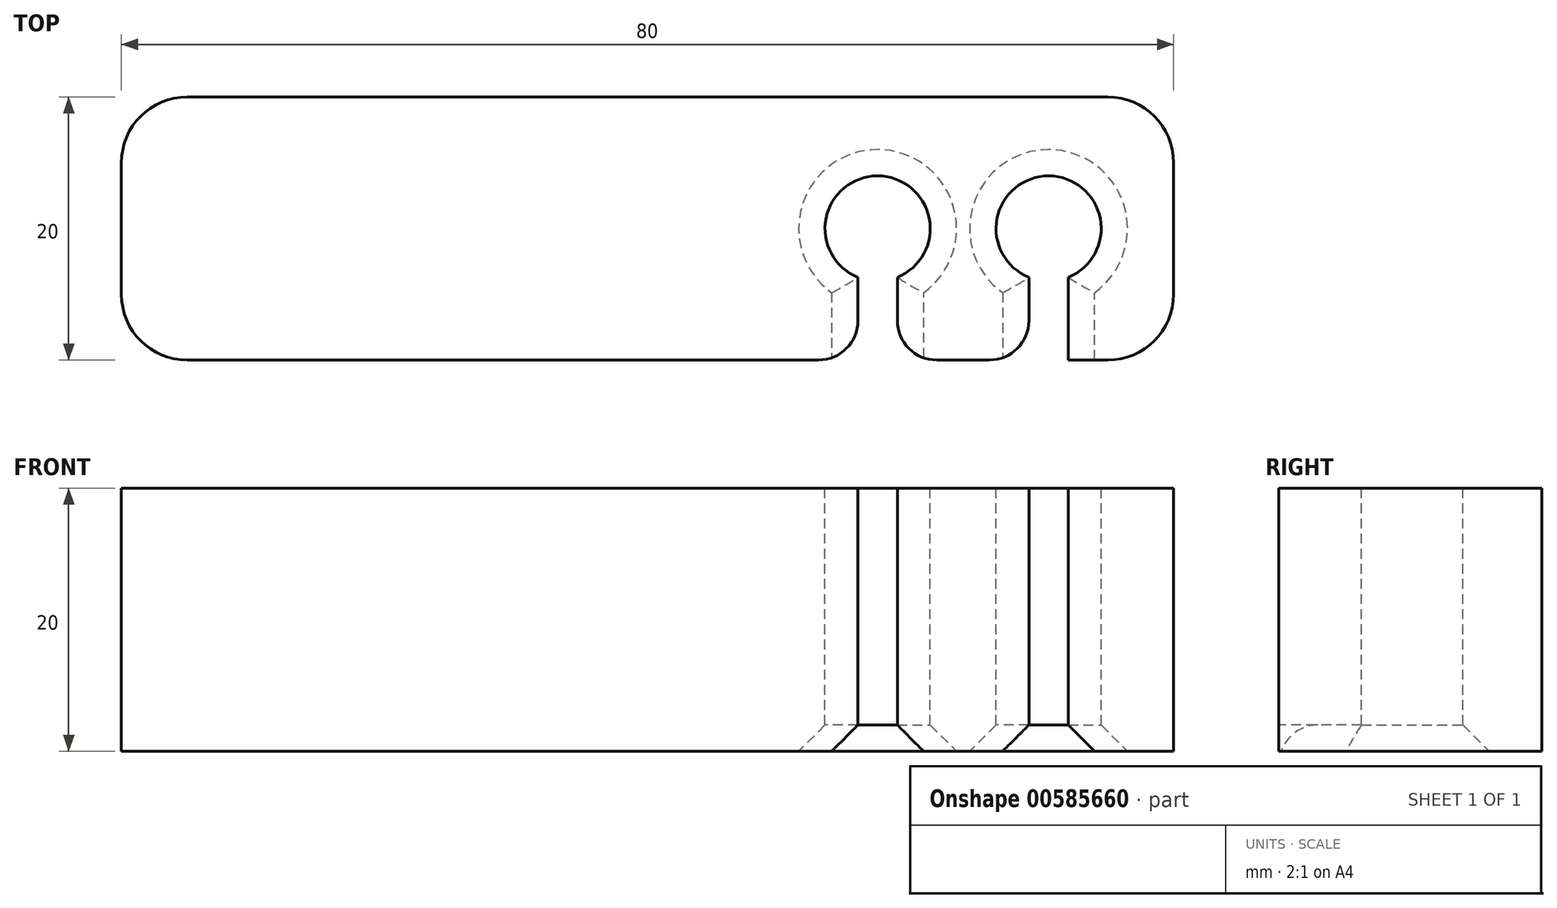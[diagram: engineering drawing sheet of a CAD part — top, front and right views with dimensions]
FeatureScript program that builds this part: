
annotation { "Feature Type Name" : "Feature", "Feature Type Description" : "" }
export const myFeature = defineFeature(function(context is Context, id is Id, definition is map)
    precondition{}
    {
        {
            var Q0;
            Q0=qCreatedBy(makeId("Top.planeOp"),FACE);
            var sketch = newSketch(context, id + "F0", { "sketchPlane" : qUnion([Q0])});
            skLineSegment(sketch, "E0.bottom", {"start": v(40, -10) * mm, "end": v(-40, -10) * mm});
            skLineSegment(sketch, "E0.top", {"start": v(40, 10) * mm, "end": v(-40, 10) * mm});
            skLineSegment(sketch, "E0.left", {"start": v(40, -10) * mm, "end": v(40, 10) * mm});
            skLineSegment(sketch, "E0.right", {"start": v(-40, -10) * mm, "end": v(-40, 10) * mm});
            skPoint(sketch, "E0.middle", {"position": v(0, 0) * mm});
            skSolve(sketch);
        }
        {
            var Q0;
            Q0 = qSketchRegion(id + "F0", true);
            extrude(context, id + "F1", {"entities" : qUnion([Q0]), "depth" : 20 * mm, "offsetDistance" : 25 * mm});
        }
        {
            var Q0;
            Q0=makeQuery(id+"F1.opExtrude","CAP_FACE",FACE,{"disambiguationData":[OSD([sQuery(id+"F0.wireOp",EDGE,"E0.bottom"),sQuery(id+"F0.wireOp",EDGE,"E0.top"),sQuery(id+"F0.wireOp",EDGE,"E0.left"),sQuery(id+"F0.wireOp",EDGE,"E0.right")])],"isStart":false});
            var sketch = newSketch(context, id + "F2", { "sketchPlane" : qUnion([Q0])});
            skLineSegment(sketch, "E1.bottom", {"start": v(32, -10) * mm, "end": v(29, -10) * mm});
            skLineSegment(sketch, "E1.top", {"start": v(32, 0) * mm, "end": v(29, 0) * mm, "construction": true});
            skLineSegment(sketch, "E1.left", {"start": v(32, -10) * mm, "end": v(32, 0) * mm});
            skLineSegment(sketch, "E1.right", {"start": v(29, -10) * mm, "end": v(29, 0) * mm});
            skLineSegment(sketch, "E2.bottom", {"start": v(19, -10) * mm, "end": v(16, -10) * mm});
            skLineSegment(sketch, "E2.top", {"start": v(19, 0) * mm, "end": v(16, 0) * mm, "construction": true});
            skLineSegment(sketch, "E2.left", {"start": v(19, -10) * mm, "end": v(19, 0) * mm});
            skLineSegment(sketch, "E2.right", {"start": v(16, -10) * mm, "end": v(16, 0) * mm});
            skLineSegment(sketch, "E3", {"start": v(19, 0) * mm, "end": v(29, 0) * mm, "construction": true});
            skArc(sketch, "E4", {"start": v(19, 0) * mm, "mid": v(17.5, 1.5) * mm, "end": v(16, 0) * mm});
            skArc(sketch, "E5", {"start": v(32, 0) * mm, "mid": v(30.5, 1.5) * mm, "end": v(29, 0) * mm});
            skSolve(sketch);
        }
        {
            var Q0;
            Q0 = qSketchRegion(id + "F2", true);
            extrude(context, id + "F3", {"entities" : qUnion([Q0]), "operationType" : NewBodyOperationType.REMOVE, "endBound" : BoundingType.THROUGH_ALL, "oppositeDirection" : true, "depth" : 25 * mm, "offsetDistance" : 25 * mm});
        }
        {
            var Q0;
            Q0=makeQuery(id+"F1.opExtrude","CAP_FACE",FACE,{"disambiguationData":[OSD([sQuery(id+"F0.wireOp",EDGE,"E0.bottom"),sQuery(id+"F0.wireOp",EDGE,"E0.top"),sQuery(id+"F0.wireOp",EDGE,"E0.left"),sQuery(id+"F0.wireOp",EDGE,"E0.right")])],"isStart":false});
            var sketch = newSketch(context, id + "F4", { "sketchPlane" : qUnion([Q0])});
            skCircle(sketch, "E6", {"center": v(17.5, 0) * mm, "radius": 4 * mm});
            skCircle(sketch, "E7", {"center": v(30.5, 0) * mm, "radius": 4 * mm});
            skSolve(sketch);
        }
        {
            var Q0;
            Q0 = qSketchRegion(id + "F4", true);
            extrude(context, id + "F5", {"entities" : qUnion([Q0]), "operationType" : NewBodyOperationType.REMOVE, "endBound" : BoundingType.THROUGH_ALL, "oppositeDirection" : true, "depth" : 25 * mm, "offsetDistance" : 25 * mm});
        }
        {
            var Q0;
            Q0=makeQuery(id+"F5.boolean.opBoolean","COPY",EDGE,{"derivedFrom":makeQuery(id+"F5.opExtrude","CAP_EDGE",EDGE,{"disambiguationData":[OSD([sQuery(id+"F4.wireOp",EDGE,"E6")])],"isStart":true})});
            var Q1;
            Q1=makeQuery(id+"F5.boolean.opBoolean","COPY",EDGE,{"derivedFrom":makeQuery(id+"F5.opExtrude","CAP_EDGE",EDGE,{"disambiguationData":[OSD([sQuery(id+"F4.wireOp",EDGE,"E7")])],"isStart":true})});
            var Q2;
            Q2=makeQuery(id+"F5.boolean.opBoolean","INTERSECT",EDGE,{"derivedFrom":[makeQuery(id+"F1.opExtrude","CAP_FACE",FACE,{"disambiguationData":[OSD([sQuery(id+"F0.wireOp",EDGE,"E0.bottom"),sQuery(id+"F0.wireOp",EDGE,"E0.top"),sQuery(id+"F0.wireOp",EDGE,"E0.left"),sQuery(id+"F0.wireOp",EDGE,"E0.right")])],"isStart":true}),makeQuery(id+"F5.opExtrude","SWEPT_FACE",FACE,{"disambiguationData":[OSD([sQuery(id+"F4.wireOp",EDGE,"E6")])]})]});
            var Q3;
            Q3=makeQuery(id+"F5.boolean.opBoolean","INTERSECT",EDGE,{"derivedFrom":[makeQuery(id+"F1.opExtrude","CAP_FACE",FACE,{"disambiguationData":[OSD([sQuery(id+"F0.wireOp",EDGE,"E0.bottom"),sQuery(id+"F0.wireOp",EDGE,"E0.top"),sQuery(id+"F0.wireOp",EDGE,"E0.left"),sQuery(id+"F0.wireOp",EDGE,"E0.right")])],"isStart":true}),makeQuery(id+"F5.opExtrude","SWEPT_FACE",FACE,{"disambiguationData":[OSD([sQuery(id+"F4.wireOp",EDGE,"E7")])]})]});
            var Q4;
            Q4=makeQuery(id+"F3.boolean.opBoolean","COPY",EDGE,{"derivedFrom":makeQuery(id+"F3.opExtrude","CAP_EDGE",EDGE,{"disambiguationData":[OSD([sQuery(id+"F2.wireOp",EDGE,"E2.right")])],"isStart":true})});
            var Q5;
            Q5=makeQuery(id+"F3.boolean.opBoolean","COPY",EDGE,{"derivedFrom":makeQuery(id+"F3.opExtrude","CAP_EDGE",EDGE,{"disambiguationData":[OSD([sQuery(id+"F2.wireOp",EDGE,"E2.left")])],"isStart":true})});
            var Q6;
            Q6=makeQuery(id+"F3.boolean.opBoolean","COPY",EDGE,{"derivedFrom":makeQuery(id+"F3.opExtrude","CAP_EDGE",EDGE,{"disambiguationData":[OSD([sQuery(id+"F2.wireOp",EDGE,"E1.right")])],"isStart":true})});
            var Q7;
            Q7=makeQuery(id+"F3.boolean.opBoolean","COPY",EDGE,{"derivedFrom":makeQuery(id+"F3.opExtrude","CAP_EDGE",EDGE,{"disambiguationData":[OSD([sQuery(id+"F2.wireOp",EDGE,"E1.left")])],"isStart":true})});
            var Q8;
            Q8=makeQuery(id+"F3.boolean.opBoolean","INTERSECT",EDGE,{"derivedFrom":[makeQuery(id+"F1.opExtrude","CAP_FACE",FACE,{"disambiguationData":[OSD([sQuery(id+"F0.wireOp",EDGE,"E0.bottom"),sQuery(id+"F0.wireOp",EDGE,"E0.top"),sQuery(id+"F0.wireOp",EDGE,"E0.left"),sQuery(id+"F0.wireOp",EDGE,"E0.right")])],"isStart":true}),makeQuery(id+"F3.opExtrude","SWEPT_FACE",FACE,{"disambiguationData":[OSD([sQuery(id+"F2.wireOp",EDGE,"E2.right")])]})]});
            var Q9;
            Q9=makeQuery(id+"F3.boolean.opBoolean","INTERSECT",EDGE,{"derivedFrom":[makeQuery(id+"F1.opExtrude","CAP_FACE",FACE,{"disambiguationData":[OSD([sQuery(id+"F0.wireOp",EDGE,"E0.bottom"),sQuery(id+"F0.wireOp",EDGE,"E0.top"),sQuery(id+"F0.wireOp",EDGE,"E0.left"),sQuery(id+"F0.wireOp",EDGE,"E0.right")])],"isStart":true}),makeQuery(id+"F3.opExtrude","SWEPT_FACE",FACE,{"disambiguationData":[OSD([sQuery(id+"F2.wireOp",EDGE,"E2.left")])]})]});
            var Q10;
            Q10=makeQuery(id+"F3.boolean.opBoolean","INTERSECT",EDGE,{"derivedFrom":[makeQuery(id+"F1.opExtrude","CAP_FACE",FACE,{"disambiguationData":[OSD([sQuery(id+"F0.wireOp",EDGE,"E0.bottom"),sQuery(id+"F0.wireOp",EDGE,"E0.top"),sQuery(id+"F0.wireOp",EDGE,"E0.left"),sQuery(id+"F0.wireOp",EDGE,"E0.right")])],"isStart":true}),makeQuery(id+"F3.opExtrude","SWEPT_FACE",FACE,{"disambiguationData":[OSD([sQuery(id+"F2.wireOp",EDGE,"E1.right")])]})]});
            var Q11;
            Q11=makeQuery(id+"F3.boolean.opBoolean","INTERSECT",EDGE,{"derivedFrom":[makeQuery(id+"F1.opExtrude","CAP_FACE",FACE,{"disambiguationData":[OSD([sQuery(id+"F0.wireOp",EDGE,"E0.bottom"),sQuery(id+"F0.wireOp",EDGE,"E0.top"),sQuery(id+"F0.wireOp",EDGE,"E0.left"),sQuery(id+"F0.wireOp",EDGE,"E0.right")])],"isStart":true}),makeQuery(id+"F3.opExtrude","SWEPT_FACE",FACE,{"disambiguationData":[OSD([sQuery(id+"F2.wireOp",EDGE,"E1.left")])]})]});
            chamfer(context, id + "F6", {"entities" : qUnion([Q0, Q1, Q2, Q3, Q4, Q5, Q6, Q7, Q8, Q9, Q10, Q11]), "width" : 2 * mm, "tangentPropagation" : true});
        }
        {
            var Q0;
            Q0=makeQuery(id+"F3.boolean.opBoolean","COPY",EDGE,{"derivedFrom":makeQuery(id+"F3.opExtrude","SWEPT_EDGE",EDGE,{"disambiguationData":[OSD([sQuery(id+"F0.wireOp",EDGE,"E0.bottom"),sQuery(id+"F2.wireOp",EDGE,"E2.bottom"),sQuery(id+"F2.wireOp",EDGE,"E2.left")])]})});
            var Q1;
            Q1=makeQuery(id+"F3.boolean.opBoolean","COPY",EDGE,{"derivedFrom":makeQuery(id+"F3.opExtrude","SWEPT_EDGE",EDGE,{"disambiguationData":[OSD([sQuery(id+"F0.wireOp",EDGE,"E0.bottom"),sQuery(id+"F2.wireOp",EDGE,"E1.bottom"),sQuery(id+"F2.wireOp",EDGE,"E1.right")])]})});
            var Q2;
            Q2=makeQuery(id+"F3.boolean.opBoolean","COPY",EDGE,{"derivedFrom":makeQuery(id+"F3.opExtrude","SWEPT_EDGE",EDGE,{"disambiguationData":[OSD([sQuery(id+"F0.wireOp",EDGE,"E0.bottom"),sQuery(id+"F2.wireOp",EDGE,"E1.bottom"),sQuery(id+"F2.wireOp",EDGE,"E1.left")])]})});
            var Q3;
            Q3=makeQuery(id+"F3.boolean.opBoolean","COPY",EDGE,{"derivedFrom":makeQuery(id+"F3.opExtrude","SWEPT_EDGE",EDGE,{"disambiguationData":[OSD([sQuery(id+"F0.wireOp",EDGE,"E0.bottom"),sQuery(id+"F2.wireOp",EDGE,"E2.bottom"),sQuery(id+"F2.wireOp",EDGE,"E2.right")])]})});
            fillet(context, id + "F7", {"entities" : qUnion([Q0, Q1, Q2, Q3]), "radius" : 3 * mm, "tangentPropagation" : true, "allowEdgeOverflow" : false});
        }
        {
            var Q0;
            Q0=makeQuery(id+"F1.opExtrude","SWEPT_EDGE",EDGE,{"disambiguationData":[OSD([sQuery(id+"F0.wireOp",EDGE,"E0.bottom"),sQuery(id+"F0.wireOp",EDGE,"E0.left")])]});
            var Q1;
            Q1=makeQuery(id+"F1.opExtrude","SWEPT_EDGE",EDGE,{"disambiguationData":[OSD([sQuery(id+"F0.wireOp",EDGE,"E0.top"),sQuery(id+"F0.wireOp",EDGE,"E0.left")])]});
            var Q2;
            Q2=makeQuery(id+"F1.opExtrude","SWEPT_EDGE",EDGE,{"disambiguationData":[OSD([sQuery(id+"F0.wireOp",EDGE,"E0.top"),sQuery(id+"F0.wireOp",EDGE,"E0.right")])]});
            var Q3;
            Q3=makeQuery(id+"F1.opExtrude","SWEPT_EDGE",EDGE,{"disambiguationData":[OSD([sQuery(id+"F0.wireOp",EDGE,"E0.bottom"),sQuery(id+"F0.wireOp",EDGE,"E0.right")])]});
            fillet(context, id + "F8", {"entities" : qUnion([Q0, Q1, Q2, Q3]), "radius" : 5 * mm, "tangentPropagation" : true, "allowEdgeOverflow" : false});
        }
    });
